# Revit family: Konsole 35- 21
name_source: partatom
category: HLS-Bauteile
revit_build: Autodesk Revit 2017 (Build: 20190507_1515(x64)
units: mm (PartAtom-declared; Revit-internal decimal feet)

## family parameters
Basisbauteil = Fläche
Beim Laden mit Abzugskörper schneiden = Nein
Bemaßung runder Anschluss = Durchmesser verwenden
Gemeinsam genutzt = Ja
Raumberechnungspunkt = Nein
Teiletyp = Normal

## types (6) — shared parameters
Ausrichtung Platte = längs
Breite Platte = 40 mm  [stored 0.131234 ft]
Breite Profil = 35 mm  [stored 0.114829 ft]
Fabrikat = MEFA
Firma = MEFA Befestigungs- und Montagesysteme GmbH
Höhe Profil = 21 mm  [stored 0.0688976 ft]
Kurztext1 = Konsole C-Profil 35/21
Langloch Platte = 11x15 mm
Lochabstand = 55 mm
Länge Platte = 86 mm  [stored 0.282152 ft]
Material = Stahl
Materialname C-Profil = S235JR
Materialname Platte = S235JR
Oberflaeche = galvanisch verzinkt
Profil = C-Profil
Stärke Platte = 5 mm  [stored 0.0164042 ft]
Stärke Profil = 2 mm  [stored 0.00656168 ft]
Vorgabe-Ansicht = 1219 mm

## per-type parameters (varying)
| type | Artikelnummer | EAN | Gewicht | Gewicht pro Bauteil | Kurztext2 | Länge Konsole | Schienenlänge | max. zul. Last F1 | max. zul. Last F2 | max. zul. Last q0 |
| Konsole 35- 21 L=  525 Platte längs gvz | 18020525 | 4250928437501 | 0.73 kg | 0.73 kg | L= 525 mm Platte längs gvz | 525 mm | Montageschiene 35- 21-2,0 für Konsole : C-Profil 35- 21-2,0 L=  525 | 0.08 kip | 0.03 kip | 0.042 kip/ft |
| Konsole 35- 21 L=  420 Platte längs gvz | 18020420 | 4250928437495 | 0.61 kg | 0.61 kg | L= 420 mm Platte längs gvz | 420 mm  [stored 1.37795 ft] | Montageschiene 35- 21-2,0 für Konsole : C-Profil 35- 21-2,0 L=  420 | 0.10 kip | 0.04 kip | 0.073 kip/ft |
| Konsole 35- 21 L=  315 Platte längs gvz | 18020315 | 4250928437488 | 0.49 kg | 0.49 kg | L= 315 mm Platte längs gvz | 315 mm  [stored 1.03346 ft] | Montageschiene 35- 21-2,0 für Konsole : C-Profil 35- 21-2,0 L=  315 | 0.13 kip | 0.07 kip | 0.130 kip/ft |
| Konsole 35- 21 L=  262,5 Platte längs gvz | 18020263 | 4250928437471 | 0.43 kg | 0.43 kg | L= 262,5 mm Platte längs gvz | 263 mm | Montageschiene 35- 21-2,0 für Konsole : C-Profil 35- 21-2,0 L=  262,5 | 0.16 kip | 0.08 kip | 0.186 kip/ft |
| Konsole 35- 21 L=  210 Platte längs gvz | 18020210 | 4250928437464 | 0.37 kg | 0.37 kg | L= 210 mm Platte längs gvz | 210 mm  [stored 0.688976 ft] | Montageschiene 35- 21-2,0 für Konsole : C-Profil 35- 21-2,0 L=  210 | 0.20 kip | 0.10 kip | 0.292 kip/ft |
| Konsole 35- 21 L=  157,5 Platte längs gvz | 18020158 | 4250928437457 | 0.31 kg | 0.31 kg | L= 157,5 mm Platte längs gvz | 158 mm | Montageschiene 35- 21-2,0 für Konsole : C-Profil 35- 21-2,0 L=  157,5 | 0.27 kip | 0.13 kip | 0.519 kip/ft |

note: [stored X ft] marks values corroborated as IEEE doubles in the binary element streams (Revit-internal decimal feet)
